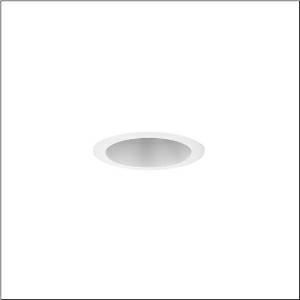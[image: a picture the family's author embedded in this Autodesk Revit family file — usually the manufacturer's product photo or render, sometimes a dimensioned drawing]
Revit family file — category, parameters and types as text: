
# Revit family: lunis_31-l_51dn15me41b
name_source: partatom
category: Lighting Fixtures
units: mm (PartAtom-declared; Revit-internal decimal feet)

## family parameters
Cut with Voids When Loaded = No
Host = Face
Light Source = No
Part Type = Normal
Room Calculation Point = No
Round Connector Dimension = Use Diameter
Shared = No

## types (1)
- --- (1 x LED, 1700 lm, 12 W, 4000K)
    Apparent Load = 12 VA
    CIE Flux Codes = 93 98 100 100 100
    Color Rendering = 80
    Color Temperature = 4000K
    Default Elevation = 1800 mm
    Description = Lunis 31-L, downlight, light control with reflector, light emission: direct distribution, LED rated luminous flux: 1.700lm, light colour: 840, mains connection: 220..240V, AC/DC, 0/50..60Hz, housing, of aluminium, white, protection rating (complete): IP20, protection rating (on room side): IP54, insulation class (complete): insulation class II (safety insulation), certification: CE, ENEC, packaging unit: 1 piece
    Height = 0 mm  [stored 0 ft]
    Lamp = 1 x LED
    Lamp Light Flux = 1700 lm
    Lamp Power = 12 W
    Lamp count = 1
    Length = 188 mm  [stored 0.616798 ft]
    Luminous efficacy = 142 lm/W
    Manufacturer = Siteco
    ModVariant = No
    Model = 51DN15ME41B
    Mounting Place = Ceiling
    Mounting Type = Recessed
    Number of Poles = 1
    OnlyDefault = Yes
    Power Factor = 1
    Product Name = Lunis 31-L
    Product group = downlight
    ProductGroupID = 401
    Protection Class = Protection class II
    Protection Degree = IP 20
    RLX_Detail_Level = 1
    RLX_Emergency_Light_Flux = 0 lm
    RLX_Emergency_Type = 0
    RLX_Emergency_Type_DB = No
    RlxData = <blob elided: 22265 chars, md5=2b0ebeaf>
    Socket = socket
    Standby Power = 0 W
    System Light Flux = 1700 lm
    System Power = 12 W
    Type Comments = individual setting: luminous flux: 100 % | (OFF | ON) | 300 mA
    Type Image = l_1345911.jpg
    URL = http://relux.com
    VarID = @adj_029675
    Voltage = 0 V
    Weight = 0.00 kg
    Width = 0 mm  [stored 0 ft]

note: [stored X ft] marks values corroborated as IEEE doubles in the binary element streams (Revit-internal decimal feet)

## geometry (parser evidence)
native form markers: Blend x4, Sweep x10
no freeform markers — native parametric forms only
